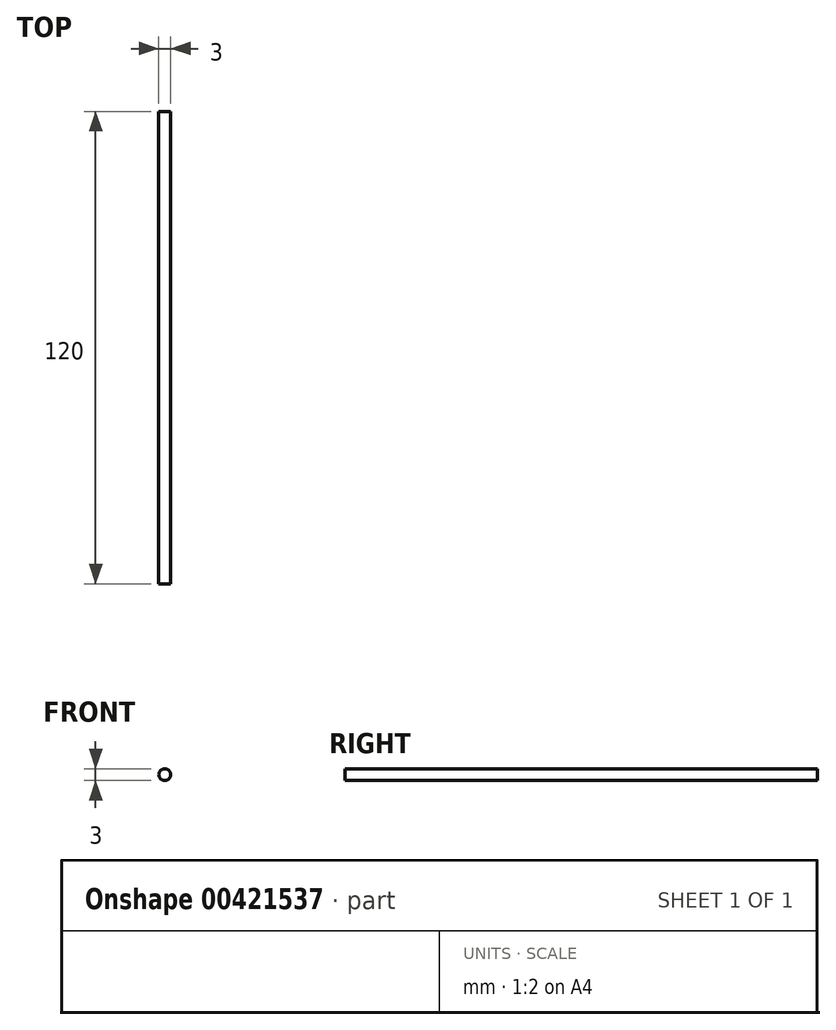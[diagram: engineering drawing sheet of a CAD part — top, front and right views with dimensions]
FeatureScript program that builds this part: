
annotation { "Feature Type Name" : "Feature", "Feature Type Description" : "" }
export const myFeature = defineFeature(function(context is Context, id is Id, definition is map)
    precondition{}
    {
        {
            var Q0;
            Q0=qCreatedBy(makeId("Front.planeOp"),FACE);
            var sketch = newSketch(context, id + "F0", { "sketchPlane" : qUnion([Q0])});
            skCircle(sketch, "E0", {"center": v(0, 0) * mm, "radius": 1.5 * mm});
            skSolve(sketch);
        }
        {
            var Q0;
            Q0 = qSketchRegion(id + "F0", true);
            extrude(context, id + "F1", {"entities" : qUnion([Q0]), "depth" : 120 * mm});
        }
    });
